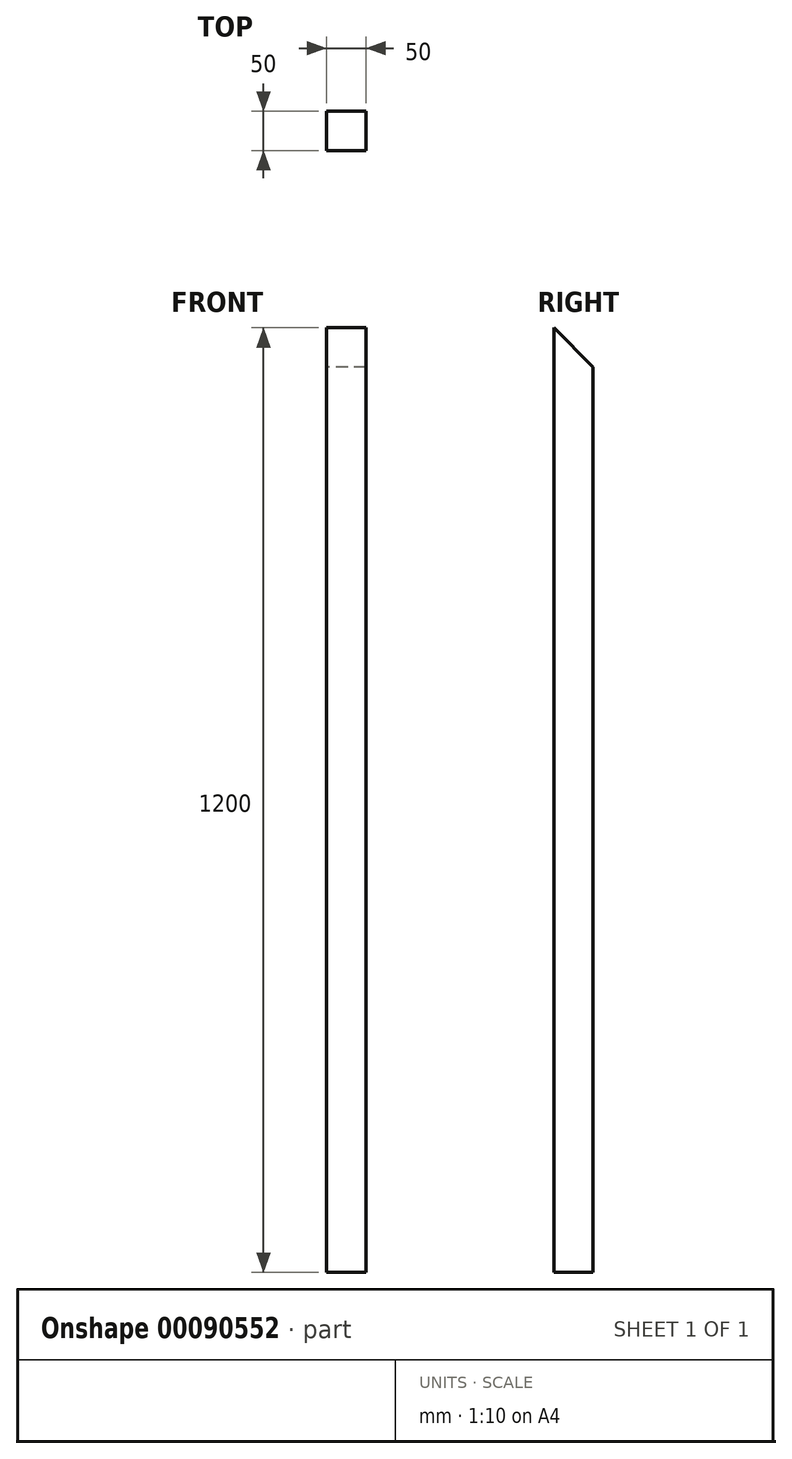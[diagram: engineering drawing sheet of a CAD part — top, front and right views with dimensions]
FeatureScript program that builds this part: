
annotation { "Feature Type Name" : "Feature", "Feature Type Description" : "" }
export const myFeature = defineFeature(function(context is Context, id is Id, definition is map)
    precondition{}
    {
        {
            var Q0;
            Q0=qCreatedBy(makeId("Top.planeOp"),FACE);
            var sketch = newSketch(context, id + "F0", { "sketchPlane" : qUnion([Q0])});
            skLineSegment(sketch, "E0.bottom", {"start": v(25, -25) * mm, "end": v(-25, -25) * mm});
            skLineSegment(sketch, "E0.top", {"start": v(25, 25) * mm, "end": v(-25, 25) * mm});
            skLineSegment(sketch, "E0.left", {"start": v(25, -25) * mm, "end": v(25, 25) * mm});
            skLineSegment(sketch, "E0.right", {"start": v(-25, -25) * mm, "end": v(-25, 25) * mm});
            skPoint(sketch, "E0.middle", {"position": v(0, 0) * mm});
            skSolve(sketch);
        }
        {
            var Q0;
            Q0=qSketchRegion(id+"F0",true);
            extrude(context, id + "F1", {"entities" : qUnion([Q0]), "depth" : 1200 * mm});
        }
        {
            var Q0;
            Q0=qCreatedBy(makeId("Right.planeOp"),FACE);
            var sketch = newSketch(context, id + "F2", { "sketchPlane" : qUnion([Q0])});
            skLineSegment(sketch, "E1", {"start": v(-25, 1200) * mm, "end": v(135.3, 1200) * mm});
            skLineSegment(sketch, "E2", {"start": v(135.3, 1200) * mm, "end": v(135.3, 1039.7) * mm});
            skLineSegment(sketch, "E3", {"start": v(135.3, 1039.7) * mm, "end": v(-25, 1200) * mm});
            skSolve(sketch);
        }
        {
            var Q0;
            Q0=qSketchRegion(id+"F2",true);
            extrude(context, id + "F3", {"entities" : qUnion([Q0]), "operationType" : NewBodyOperationType.REMOVE, "endBound" : BoundingType.THROUGH_ALL, "oppositeDirection" : true, "depth" : 25 * mm, "hasSecondDirection" : true, "secondDirectionBound" : SecondDirectionBoundingType.THROUGH_ALL, "secondDirectionOppositeDirection" : false, "secondDirectionDepth" : 25 * mm});
        }
    });
